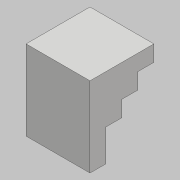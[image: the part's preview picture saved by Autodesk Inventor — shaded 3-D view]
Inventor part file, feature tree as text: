
AUTODESK INVENTOR PART (.ipt)
format: ipt  version: 2018 (Build 220112000, 112)  size: 109,056 bytes
history: native  units: mm
features: extrude x4, sketch x3, other x1, projected_geometry x1
ambient origin geometry x8: Origin, YZ Plane, XZ Plane, XY Plane, X Axis, Y Axis, Z Axis, Center Point
bodies: Body1 (feature_tree)
feature tree (9):
  other  "實體1"
  extrude  "擠出1"  Depth=4.0mm
  sketch  "草圖2"
  extrude  "擠出2"  Depth=5.0mm
  extrude  "擠出3"  Depth=4.0mm TaperAngle=0.0deg
  extrude  "擠出4"  Depth=2.0mm
  sketch  "草圖1"
  sketch  "草圖3"
  projected_geometry  "投影迴路1"
